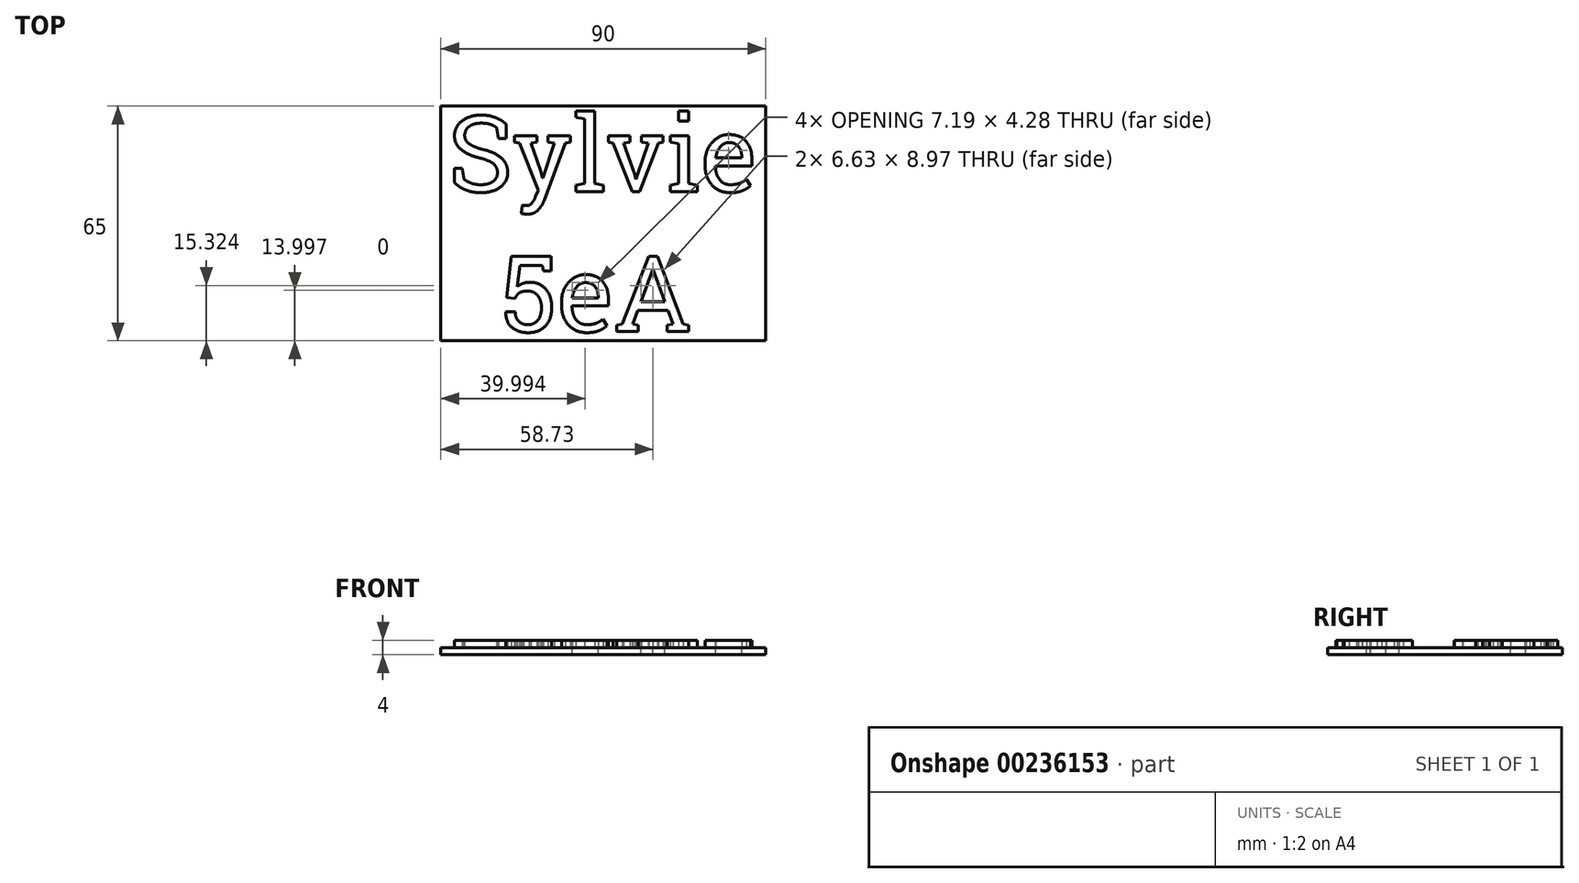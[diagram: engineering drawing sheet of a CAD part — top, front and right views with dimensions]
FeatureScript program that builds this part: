
annotation { "Feature Type Name" : "Feature", "Feature Type Description" : "" }
export const myFeature = defineFeature(function(context is Context, id is Id, definition is map)
    precondition{}
    {
        {
            var Q0;
            Q0=qCreatedBy(makeId("Top.planeOp"),FACE);
            var sketch = newSketch(context, id + "F0", { "sketchPlane" : qUnion([Q0])});
            skLineSegment(sketch, "E0.bottom", {"start": v(0, 0) * mm, "end": v(90, 0) * mm});
            skLineSegment(sketch, "E0.top", {"start": v(0, -65) * mm, "end": v(90, -65) * mm});
            skLineSegment(sketch, "E0.left", {"start": v(0, 0) * mm, "end": v(0, -65) * mm});
            skLineSegment(sketch, "E0.right", {"start": v(90, 0) * mm, "end": v(90, -65) * mm});
            skSolve(sketch);
        }
        {
            var Q0;
            Q0=makeQuery(id+"F0.imprint","IMPRINT",FACE,{"disambiguationData":[TD([[makeQuery(id+"F0.imprint","IMPRINT",EDGE,{"derivedFrom":sQuery(id+"F0.wireOp",EDGE,"E0.bottom")}),-1.0]])]});
            var sketch = newSketch(context, id + "F1", { "sketchPlane" : qUnion([Q0])});
            skText(sketch, "E1", { "text": "Sylvie \n  5eA", "fontName": "RobotoSlab-Regular.ttf"});
            const initialGuessF1  = {"E1": [0.002, -0.02366, 1, 0, 0.02116]};
            skSetInitialGuess(sketch, initialGuessF1);
            skSolve(sketch);
        }
        {
            var Q0;
            Q0 = qSketchRegion(id + "F1", true);
            var Q1;
            Q1=makeQuery(id+"F1.imprint","IMPRINT",FACE,{"disambiguationData":[TD([[makeQuery(id+"F1.imprint","IMPRINT",EDGE,{"derivedFrom":sQuery(id+"F1.wireOp",EDGE,"E1.sketch_text.stroke-0")}),1.0]])]});
            extrude(context, id + "F2", {"entities" : qUnion([Q0, Q1]), "oppositeDirection" : true, "depth" : 2 * mm});
        }
        {
            var Q0;
            Q0 = qSketchRegion(id + "F1", true);
            extrude(context, id + "F3", {"entities" : qUnion([Q0]), "depth" : 2 * mm});
        }
    });
